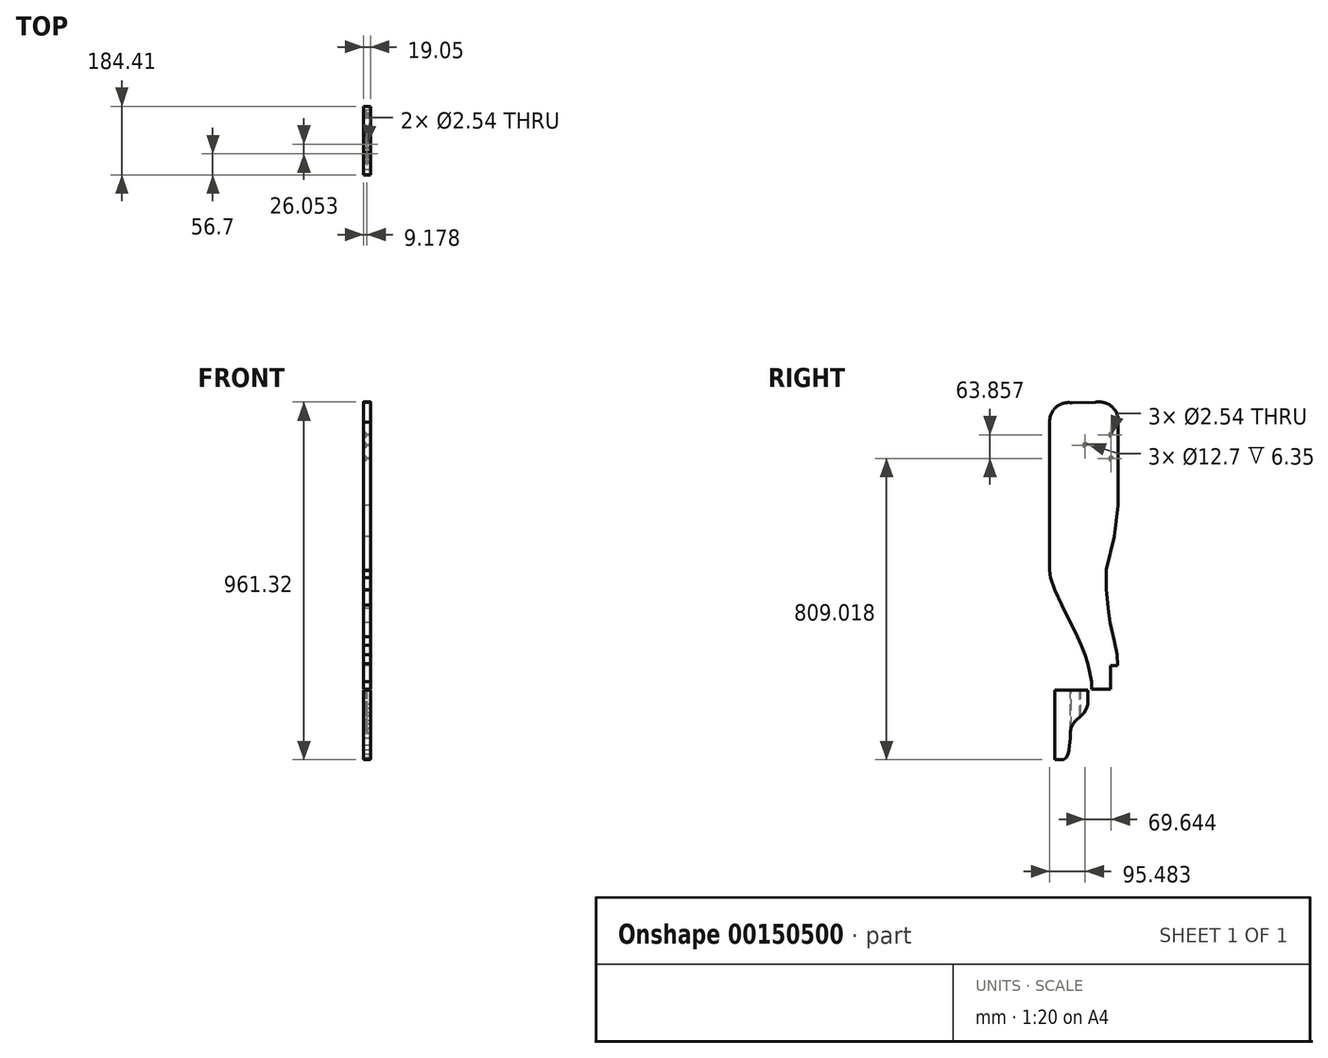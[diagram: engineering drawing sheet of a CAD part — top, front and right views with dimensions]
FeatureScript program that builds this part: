
annotation { "Feature Type Name" : "Feature", "Feature Type Description" : "" }
export const myFeature = defineFeature(function(context is Context, id is Id, definition is map)
    precondition{}
    {
        {
            var Q0;
            Q0=qCreatedBy(makeId("Right.planeOp"),FACE);
            var sketch = newSketch(context, id + "F0", { "sketchPlane" : qUnion([Q0])});
            skArc(sketch, "E0", {"start": v(-9.46, 75.88) * mm, "mid": v(-26, 118.46) * mm, "end": v(-70.06, 130.54) * mm});
            skArc(sketch, "E1", {"start": v(-132.5, 128.84) * mm, "mid": v(-175.59, 117.94) * mm, "end": v(-193.61, 77.32) * mm});
            skLineSegment(sketch, "E2", {"start": v(-70.06, 130.54) * mm, "end": v(-132.5, 128.84) * mm});
            skLineSegment(sketch, "E3", {"start": v(-9.46, -145.88) * mm, "end": v(-9.46, 75.88) * mm});
            skLineSegment(sketch, "E4", {"start": v(-193.61, 77.32) * mm, "end": v(-193.61, -321.25) * mm});
            skLineSegment(sketch, "E5", {"start": v(-10.8, -577.01) * mm, "end": v(-29.84, -577.01) * mm});
            skLineSegment(sketch, "E6", {"start": v(-9.46, -145.88) * mm, "end": v(-19.66, -230.65) * mm});
            skLineSegment(sketch, "E7", {"start": v(-19.66, -230.65) * mm, "end": v(-41.21, -318.93) * mm});
            skLineSegment(sketch, "E8", {"start": v(-41.21, -318.93) * mm, "end": v(-41.21, -370.76) * mm});
            skLineSegment(sketch, "E9", {"start": v(-41.21, -370.76) * mm, "end": v(-36.8, -423.85) * mm});
            skLineSegment(sketch, "E10", {"start": v(-36.8, -423.85) * mm, "end": v(-30.98, -461.78) * mm});
            skLineSegment(sketch, "E11", {"start": v(-30.98, -461.78) * mm, "end": v(-20.05, -510.64) * mm});
            skLineSegment(sketch, "E12", {"start": v(-20.05, -510.64) * mm, "end": v(-12.2, -547.2) * mm});
            skLineSegment(sketch, "E13", {"start": v(-12.2, -547.2) * mm, "end": v(-10.8, -577.01) * mm});
            skLineSegment(sketch, "E14", {"start": v(-29.84, -640.51) * mm, "end": v(-29.84, -577.01) * mm});
            skLineSegment(sketch, "E15", {"start": v(-87.3, -588.8) * mm, "end": v(-91.04, -571.55) * mm});
            skLineSegment(sketch, "E16", {"start": v(-91.04, -571.55) * mm, "end": v(-98.51, -548.28) * mm});
            skLineSegment(sketch, "E17", {"start": v(-98.51, -548.28) * mm, "end": v(-108.2, -522.94) * mm});
            skLineSegment(sketch, "E18", {"start": v(-108.2, -522.94) * mm, "end": v(-119.14, -499.02) * mm});
            skLineSegment(sketch, "E19", {"start": v(-119.14, -499.02) * mm, "end": v(-161.16, -414.63) * mm});
            skLineSegment(sketch, "E20", {"start": v(-161.16, -414.63) * mm, "end": v(-179.94, -373.8) * mm});
            skLineSegment(sketch, "E21", {"start": v(-179.94, -373.8) * mm, "end": v(-190.87, -340.66) * mm});
            skLineSegment(sketch, "E22", {"start": v(-190.87, -340.66) * mm, "end": v(-193.61, -321.25) * mm});
            skLineSegment(sketch, "E23", {"start": v(-101.28, 129.69) * mm, "end": v(-98.16, 15.43) * mm, "construction": true});
            skLineSegment(sketch, "E24", {"start": v(-98.16, 15.43) * mm, "end": v(-9.46, 17.85) * mm, "construction": true});
            skLineSegment(sketch, "E25", {"start": v(-9.46, 43.1) * mm, "end": v(-28.51, 43.1) * mm, "construction": true});
            skPoint(sketch, "E26", {"position": v(-28.34, 17.34) * mm});
            skPoint(sketch, "E27", {"position": v(-53.8, 16.64) * mm});
            skPoint(sketch, "E28", {"position": v(-88.41, 15.7) * mm});
            skPoint(sketch, "E29", {"position": v(-28.51, -20.76) * mm});
            skLineSegment(sketch, "E30", {"start": v(-98.16, 15.43) * mm, "end": v(-193.61, 12.83) * mm, "construction": true});
            skLineSegment(sketch, "E31", {"start": v(-193.61, 12.83) * mm, "end": v(-142.83, 14.21) * mm});
            skPoint(sketch, "E32", {"position": v(-142.83, 14.21) * mm});
            skLineSegment(sketch, "E33", {"start": v(-87.3, -588.8) * mm, "end": v(-80.64, -619.55) * mm});
            skLineSegment(sketch, "E34", {"start": v(-80.64, -619.55) * mm, "end": v(-80.64, -619.82) * mm});
            skLineSegment(sketch, "E35", {"start": v(-80.64, -619.82) * mm, "end": v(-80.64, -629.6) * mm});
            skLineSegment(sketch, "E36", {"start": v(-80.64, -629.6) * mm, "end": v(-80.64, -640.44) * mm});
            skLineSegment(sketch, "E37", {"start": v(-80.64, -640.44) * mm, "end": v(-29.84, -640.51) * mm});
            skSolve(sketch);
        }
        {
            var Q0;
            Q0 = qSketchRegion(id + "F0", true);
            extrude(context, id + "F1", {"entities" : qUnion([Q0]), "depth" : 19.05 * mm});
        }
        {
            var Q0;
            Q0=qCreatedBy(makeId("Right.planeOp"),FACE);
            var sketch = newSketch(context, id + "F2", { "sketchPlane" : qUnion([Q0])});
            skLineSegment(sketch, "E38", {"start": v(-91.54, -643.6) * mm, "end": v(-180.44, -643.6) * mm});
            skLineSegment(sketch, "E39", {"start": v(-180.44, -643.6) * mm, "end": v(-180.44, -829.78) * mm});
            skLineSegment(sketch, "E40", {"start": v(-180.44, -829.78) * mm, "end": v(-163.7, -829.78) * mm});
            skLineSegment(sketch, "E41", {"start": v(-91.54, -643.6) * mm, "end": v(-91.54, -681.07) * mm});
            skLineSegment(sketch, "E42", {"start": v(-91.54, -681.07) * mm, "end": v(-94.58, -691.9) * mm});
            skLineSegment(sketch, "E43", {"start": v(-94.58, -691.9) * mm, "end": v(-101.21, -703.64) * mm});
            skLineSegment(sketch, "E44", {"start": v(-101.21, -703.64) * mm, "end": v(-108.9, -711.93) * mm});
            skLineSegment(sketch, "E45", {"start": v(-108.9, -711.93) * mm, "end": v(-123.5, -725.03) * mm});
            skLineSegment(sketch, "E46", {"start": v(-123.5, -725.03) * mm, "end": v(-131.33, -734.22) * mm});
            skLineSegment(sketch, "E47", {"start": v(-131.33, -734.22) * mm, "end": v(-136.6, -745.78) * mm});
            skLineSegment(sketch, "E48", {"start": v(-136.6, -745.78) * mm, "end": v(-138.5, -759.4) * mm});
            skLineSegment(sketch, "E49", {"start": v(-138.5, -759.4) * mm, "end": v(-138.5, -773.04) * mm});
            skLineSegment(sketch, "E50", {"start": v(-138.5, -773.04) * mm, "end": v(-140.18, -791.2) * mm});
            skLineSegment(sketch, "E51", {"start": v(-140.18, -791.2) * mm, "end": v(-142.1, -803.88) * mm});
            skLineSegment(sketch, "E52", {"start": v(-142.1, -803.88) * mm, "end": v(-144.72, -815.35) * mm});
            skLineSegment(sketch, "E53", {"start": v(-144.72, -815.35) * mm, "end": v(-149.5, -824.2) * mm});
            skLineSegment(sketch, "E54", {"start": v(-149.5, -824.2) * mm, "end": v(-155.48, -829.46) * mm});
            skLineSegment(sketch, "E55", {"start": v(-155.48, -829.46) * mm, "end": v(-163.7, -829.78) * mm});
            skSolve(sketch);
        }
        {
            var Q0;
            Q0 = qSketchRegion(id + "F2", true);
            extrude(context, id + "F3", {"entities" : qUnion([Q0]), "depth" : 19.05 * mm});
        }
        {
            var Q0;
            Q0=makeQuery(id+"F3.opExtrude","SWEPT_FACE",FACE,{"disambiguationData":[OSD([sQuery(id+"F2.wireOp",EDGE,"E38")])]});
            var sketch = newSketch(context, id + "F4", { "sketchPlane" : qUnion([Q0])});
            skPoint(sketch, "E56", {"position": v(9.18, -110.89) * mm});
            skPoint(sketch, "E57", {"position": v(9.18, -136.94) * mm});
            skLineSegment(sketch, "E58", {"start": v(9.53, -180.44) * mm, "end": v(9.18, -91.54) * mm, "construction": true});
            skSolve(sketch);
        }
        {
            var Q0;
            Q0=sQuery(id+"F4.wireOp",VERTEX,"E57");
            var Q1;
            Q1=sQuery(id+"F4.wireOp",VERTEX,"E56");
            var Q2;
            Q2=makeQuery(id+"F3.opExtrude","SWEPT_BODY",BODY,{"disambiguationData":[OSD([sQuery(id+"F2.wireOp",EDGE,"E38"),sQuery(id+"F2.wireOp",EDGE,"E39"),sQuery(id+"F2.wireOp",EDGE,"E40"),sQuery(id+"F2.wireOp",EDGE,"E41"),sQuery(id+"F2.wireOp",EDGE,"E42"),sQuery(id+"F2.wireOp",EDGE,"E43"),sQuery(id+"F2.wireOp",EDGE,"E44"),sQuery(id+"F2.wireOp",EDGE,"E45"),sQuery(id+"F2.wireOp",EDGE,"E46"),sQuery(id+"F2.wireOp",EDGE,"E47"),sQuery(id+"F2.wireOp",EDGE,"E48"),sQuery(id+"F2.wireOp",EDGE,"E49"),sQuery(id+"F2.wireOp",EDGE,"E50"),sQuery(id+"F2.wireOp",EDGE,"E51"),sQuery(id+"F2.wireOp",EDGE,"E52"),sQuery(id+"F2.wireOp",EDGE,"E53"),sQuery(id+"F2.wireOp",EDGE,"E54"),sQuery(id+"F2.wireOp",EDGE,"E55")])]});
            hole(context, id + "F5", {"style" : HoleStyle.SIMPLE, "endStyle" : HoleEndStyle.THROUGH, "holeDiameter" : 2.54 * mm, "locations" : qUnion([Q0, Q1]), "scope" : qUnion([Q2]), "isTappedThrough" : true});
        }
        {
            var Q0;
            Q0=sQuery(id+"F0.wireOp",VERTEX,"E29");
            var Q1;
            Q1=sQuery(id+"F0.wireOp",VERTEX,"E25.end");
            var Q2;
            Q2=sQuery(id+"F0.wireOp",VERTEX,"E23.end");
            var Q3;
            Q3=makeQuery(id+"F1.opExtrude","SWEPT_BODY",BODY,{"disambiguationData":[OSD([sQuery(id+"F0.wireOp",EDGE,"E0"),sQuery(id+"F0.wireOp",EDGE,"E1"),sQuery(id+"F0.wireOp",EDGE,"E2"),sQuery(id+"F0.wireOp",EDGE,"E3"),sQuery(id+"F0.wireOp",EDGE,"E4"),sQuery(id+"F0.wireOp",EDGE,"E5"),sQuery(id+"F0.wireOp",EDGE,"oIR5Aljz-vCWG-jUG9-CAz4-xxcIfngGmacA"),sQuery(id+"F0.wireOp",EDGE,"2AJYBhot-aTbF-qlyU-3KPI-1kneUEEkDNKH"),sQuery(id+"F0.wireOp",EDGE,"E6"),sQuery(id+"F0.wireOp",EDGE,"E7"),sQuery(id+"F0.wireOp",EDGE,"E8"),sQuery(id+"F0.wireOp",EDGE,"E9"),sQuery(id+"F0.wireOp",EDGE,"E10"),sQuery(id+"F0.wireOp",EDGE,"E11"),sQuery(id+"F0.wireOp",EDGE,"E12"),sQuery(id+"F0.wireOp",EDGE,"E13"),sQuery(id+"F0.wireOp",EDGE,"E14"),sQuery(id+"F0.wireOp",EDGE,"ePQwNw62-HjoT-TKd1-s3V2-jpgCmGEpgwtA"),sQuery(id+"F0.wireOp",EDGE,"E15"),sQuery(id+"F0.wireOp",EDGE,"E16"),sQuery(id+"F0.wireOp",EDGE,"E17"),sQuery(id+"F0.wireOp",EDGE,"E18"),sQuery(id+"F0.wireOp",EDGE,"E19"),sQuery(id+"F0.wireOp",EDGE,"E20"),sQuery(id+"F0.wireOp",EDGE,"E21"),sQuery(id+"F0.wireOp",EDGE,"E22")])]});
            hole(context, id + "F6", {"style" : HoleStyle.C_BORE, "endStyle" : HoleEndStyle.THROUGH, "oppositeDirection" : true, "holeDiameter" : 2.54 * mm, "cBoreDiameter" : 12.7 * mm, "cBoreDepth" : 6.35 * mm, "locations" : qUnion([Q0, Q1, Q2]), "scope" : qUnion([Q3]), "isTappedThrough" : true});
        }
    });
